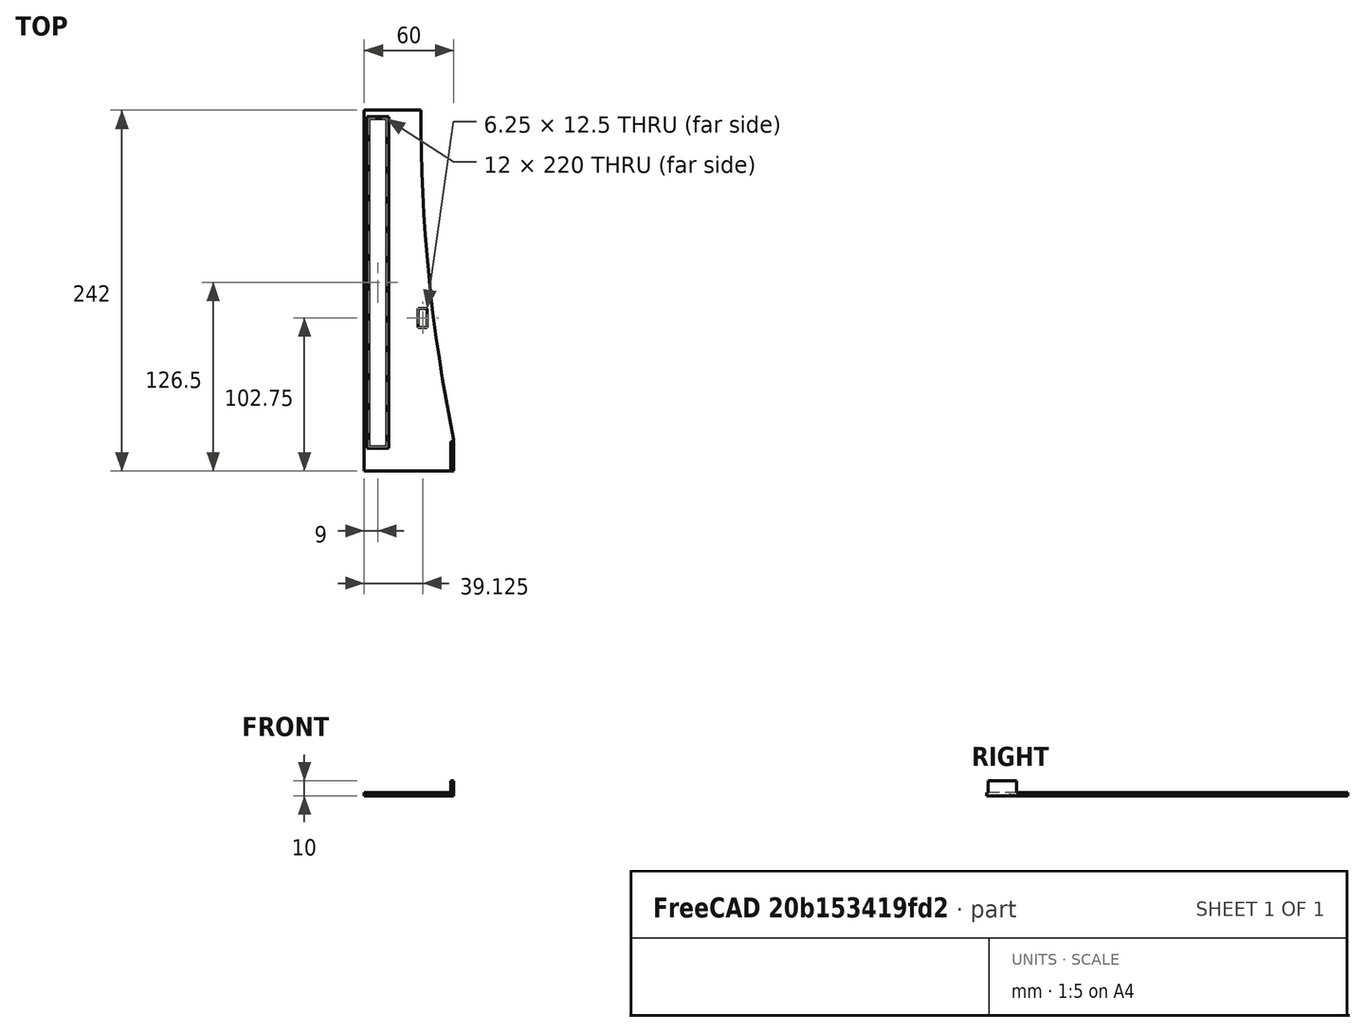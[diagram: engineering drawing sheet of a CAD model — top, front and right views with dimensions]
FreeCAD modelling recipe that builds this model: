
FCSTD DOCUMENT  (FreeCAD 0.19R)
Label: case-top
License: All rights reserved
LicenseURL: http://en.wikipedia.org/wiki/All_rights_reserved
objects: Sketcher::SketchObject×5, PartDesign::Pocket×3, PartDesign::Pad×2, Image::ImagePlane×1, PartDesign::Body×1, Mesh::Feature×1
note: 16 computed .brp shape members not serialized (recipe doc carries the construction recipe); baked Part::Feature solids carry a one-line shape summary decoded from their .brp

FEATURE [Image::ImagePlane] ImagePlane
  Placement = pos=(37,121,0) rot=(0,-1,0;3.14159rad)
  XSize = 74
  YSize = 240
FEATURE [Sketcher::SketchObject] Sketch
  FullyConstrained = true
  MapMode = 5
  Support = -> [XY_Plane]
  sketch-geometry (5):
    g0: LineSegment StartX=7 StartY=0 StartZ=0 EndX=67 EndY=0 EndZ=0
    g1: LineSegment StartX=45 StartY=242 StartZ=0 EndX=7 EndY=242 EndZ=0
    g2: LineSegment StartX=7 StartY=0 StartZ=0 EndX=7 EndY=242 EndZ=0
    g3: LineSegment StartX=67 StartY=0 StartZ=0 EndX=67 EndY=21 EndZ=0
    g4: ArcOfCircle CenterX=1119.99 CenterY=237.418 CenterZ=0 NormalX=0 NormalY=0 NormalZ=1 AngleXU=0 Radius=1075 StartAngle=3.13733 EndAngle=3.3443
  constraints (16):
    c: PointOnObject(g0,g-1)
    c: PointOnObject(g0,g-1)
    c: Horizontal(g1)
    c: Coincident(g2,g0)
    c: Coincident(g2,g1)
    c: Vertical(g2)
    c: Coincident(g3,g0)
    c: Vertical(g3)
    c: Coincident(g4,g1)
    c: Coincident(g4,g3)
    c: DistanceX(g-1,g0) = 7
    c: DistanceX(g0,g0) = 60
    c: DistanceY(g2,g2) = 242
    c: DistanceY(g3,g3) = 21
    c: DistanceX(g1,g1) = 38
    c: Diameter(g4) = 2150
FEATURE [PartDesign::Pad] Pad
  Direction = (1,1,1)
  Length = 2
  Length2 = 100
  Profile = -> Sketch
  Type = 0
FEATURE [Sketcher::SketchObject] Sketch001
  FullyConstrained = true
  MapMode = 5
  Placement = pos=(0,0,2) rot=(0,0,1;0rad)
  Support = -> [Pad]
  sketch-geometry (4):
    g0: LineSegment StartX=65 StartY=1 StartZ=0 EndX=67 EndY=1 EndZ=0
    g1: LineSegment StartX=67 StartY=1 StartZ=0 EndX=67 EndY=20 EndZ=0
    g2: LineSegment StartX=67 StartY=20 StartZ=0 EndX=65 EndY=20 EndZ=0
    g3: LineSegment StartX=65 StartY=20 StartZ=0 EndX=65 EndY=1 EndZ=0
  constraints (12):
    c: Coincident(g0,g1)
    c: Coincident(g1,g2)
    c: Coincident(g2,g3)
    c: Coincident(g3,g0)
    c: Horizontal(g0)
    c: Horizontal(g2)
    c: Vertical(g1)
    c: Vertical(g3)
    c: DistanceX(g2,g2) = 2
    c: DistanceY(g1,g1) = 19
    c: DistanceY(g-1,g0) = 1
    c: DistanceX(g-1,g0) = 65
FEATURE [PartDesign::Pad] Pad001
  BaseFeature = -> Pad
  Direction = (1,1,1)
  Length = 8
  Length2 = 100
  Profile = -> Sketch001
  Type = 0
FEATURE [Sketcher::SketchObject] Sketch002
  FullyConstrained = true
  MapMode = 5
  Placement = pos=(0,0,2) rot=(0,0,1;0rad)
  Support = -> [Pad001]
  sketch-geometry (4):
    g0: LineSegment StartX=10 StartY=16.5 StartZ=0 EndX=22 EndY=16.5 EndZ=0
    g1: LineSegment StartX=22 StartY=16.5 StartZ=0 EndX=22 EndY=236.5 EndZ=0
    g2: LineSegment StartX=22 StartY=236.5 StartZ=0 EndX=10 EndY=236.5 EndZ=0
    g3: LineSegment StartX=10 StartY=236.5 StartZ=0 EndX=10 EndY=16.5 EndZ=0
  constraints (12):
    c: Coincident(g0,g1)
    c: Coincident(g1,g2)
    c: Coincident(g2,g3)
    c: Coincident(g3,g0)
    c: Horizontal(g0)
    c: Horizontal(g2)
    c: Vertical(g1)
    c: Vertical(g3)
    c: DistanceX(g2,g2) = 12
    c: DistanceY(g1,g1) = 220
    c: DistanceX(g-1,g0) = 10
    c: DistanceY(g-1,g0) = 16.5
FEATURE [PartDesign::Pocket] Pocket
  BaseFeature = -> Pad001
  Length = 5
  Length2 = 100
  Profile = -> Sketch002
  Type = 2
FEATURE [Sketcher::SketchObject] Sketch003
  FullyConstrained = true
  MapMode = 5
  Placement = pos=(0,0,2) rot=(0,0,1;0rad)
  Support = -> [Pocket]
  sketch-geometry (4):
    g0: LineSegment StartX=8.75 StartY=15.25 StartZ=0 EndX=23.25 EndY=15.25 EndZ=0
    g1: LineSegment StartX=23.25 StartY=15.25 StartZ=0 EndX=23.25 EndY=237.75 EndZ=0
    g2: LineSegment StartX=23.25 StartY=237.75 StartZ=0 EndX=8.75 EndY=237.75 EndZ=0
    g3: LineSegment StartX=8.75 StartY=237.75 StartZ=0 EndX=8.75 EndY=15.25 EndZ=0
  constraints (12):
    c: Coincident(g0,g1)
    c: Coincident(g1,g2)
    c: Coincident(g2,g3)
    c: Coincident(g3,g0)
    c: Horizontal(g0)
    c: Horizontal(g2)
    c: Vertical(g1)
    c: Vertical(g3)
    c: DistanceX(g2,g2) = 14.5
    c: DistanceY(g1,g1) = 222.5
    c: DistanceX(g-1,g0) = 8.75
    c: DistanceY(g-1,g0) = 15.25
FEATURE [PartDesign::Pocket] Pocket001
  BaseFeature = -> Pocket
  Length = 1.45
  Length2 = 100
  Profile = -> Sketch003
  Type = 0
FEATURE [Sketcher::SketchObject] Sketch004
  FullyConstrained = true
  MapMode = 5
  Placement = pos=(0,0,2) rot=(0,0,1;0rad)
  Support = -> [Pocket001]
  sketch-geometry (4):
    g0: LineSegment StartX=43 StartY=96.5 StartZ=0 EndX=49.25 EndY=96.5 EndZ=0
    g1: LineSegment StartX=49.25 StartY=96.5 StartZ=0 EndX=49.25 EndY=109 EndZ=0
    g2: LineSegment StartX=49.25 StartY=109 StartZ=0 EndX=43 EndY=109 EndZ=0
    g3: LineSegment StartX=43 StartY=109 StartZ=0 EndX=43 EndY=96.5 EndZ=0
  constraints (12):
    c: Coincident(g0,g1)
    c: Coincident(g1,g2)
    c: Coincident(g2,g3)
    c: Coincident(g3,g0)
    c: Horizontal(g0)
    c: Horizontal(g2)
    c: Vertical(g1)
    c: Vertical(g3)
    c: DistanceX(g2,g2) = 6.25
    c: DistanceY(g1,g1) = 12.5
    c: DistanceX(g-1,g0) = 43
    c: DistanceY(g-1,g0) = 96.5
FEATURE [PartDesign::Pocket] Pocket002
  BaseFeature = -> Pocket001
  Length = 5
  Length2 = 100
  Profile = -> Sketch004
  Type = 1
FEATURE [PartDesign::Body] Body
  Group = -> [Sketch,Pad,Sketch001,Pad001,Sketch002,Pocket,Sketch003,Pocket001,Sketch004,Pocket002]
  Origin = -> Origin
  Tip = -> Pocket002
FEATURE [Mesh::Feature] Mesh  label="Body (Meshed)"
